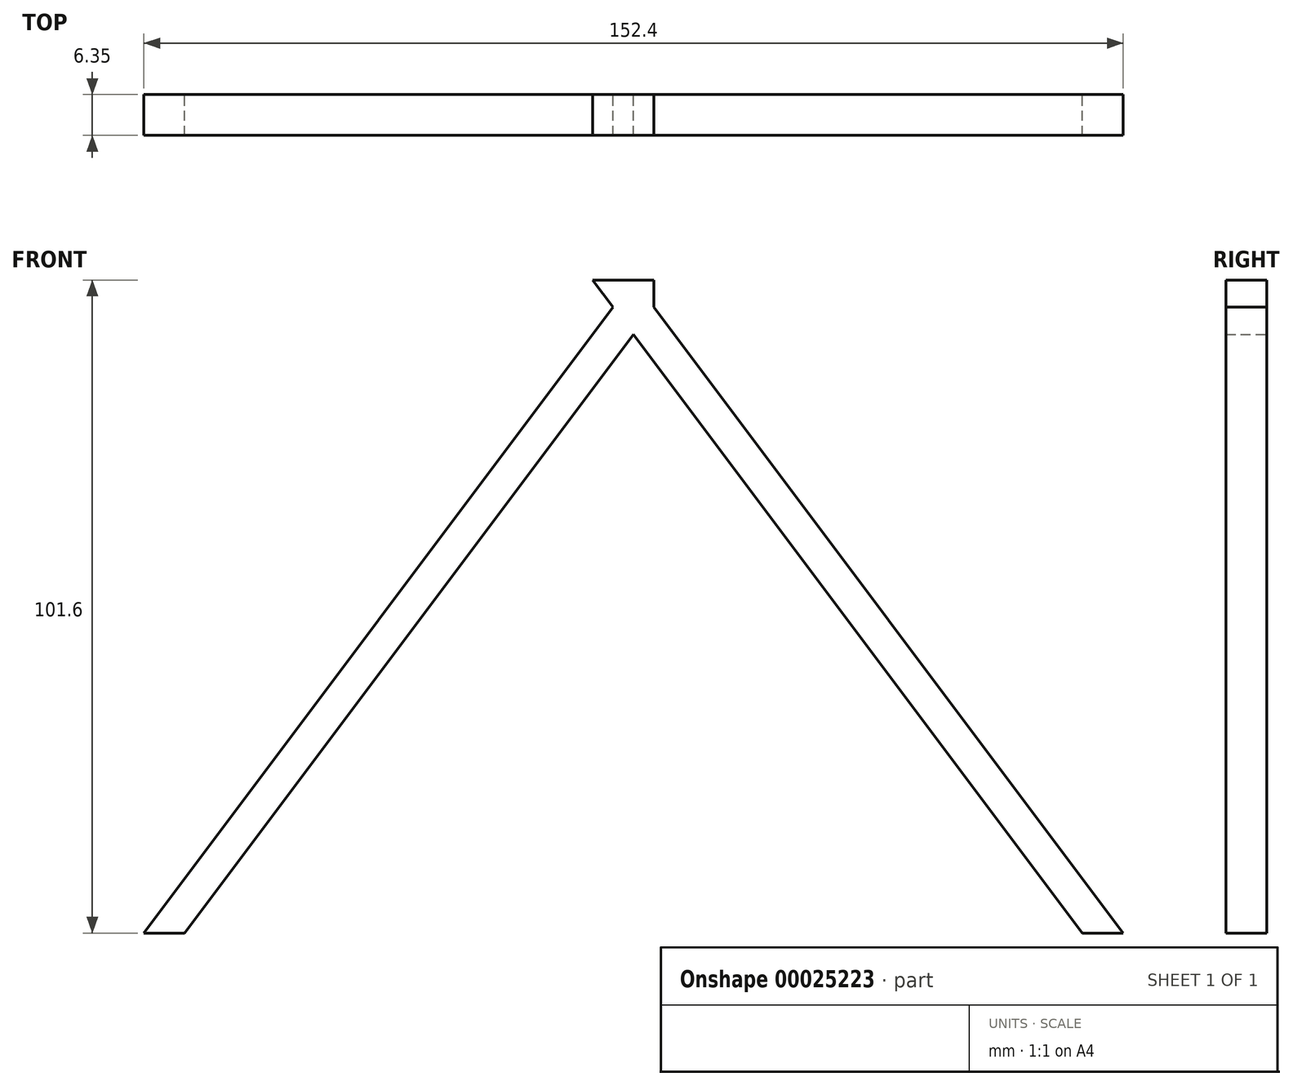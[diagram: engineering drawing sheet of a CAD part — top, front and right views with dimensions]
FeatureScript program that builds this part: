
annotation { "Feature Type Name" : "Feature", "Feature Type Description" : "" }
export const myFeature = defineFeature(function(context is Context, id is Id, definition is map)
    precondition{}
    {
        {
            var Q0;
            Q0=qCreatedBy(makeId("Front.planeOp"),FACE);
            var sketch = newSketch(context, id + "F0", { "sketchPlane" : qUnion([Q0])});
            skLineSegment(sketch, "E0", {"start": v(-76.2, 101.6) * mm, "end": v(0, 0) * mm});
            skLineSegment(sketch, "E1", {"start": v(-76.2, 101.6) * mm, "end": v(-82.55, 101.6) * mm});
            skLineSegment(sketch, "E2", {"start": v(0, 0) * mm, "end": v(-6.35, 0) * mm});
            skLineSegment(sketch, "E3", {"start": v(-6.35, 0) * mm, "end": v(-82.55, 101.6) * mm});
            skLineSegment(sketch, "E4", {"start": v(-82.55, 101.6) * mm, "end": v(-82.55, 101.6) * mm});
            skLineSegment(sketch, "E5", {"start": v(-82.55, 101.6) * mm, "end": v(-79.37, 101.6) * mm});
            skLineSegment(sketch, "E6", {"start": v(-76.2, 106.6) * mm, "end": v(-76.2, -9.76) * mm});
            skLineSegment(sketch, "E7.MirrorCS", {"start": v(-76.2, 101.6) * mm, "end": v(-152.4, 0) * mm});
            skLineSegment(sketch, "E8.MirrorCS", {"start": v(-152.4, 0) * mm, "end": v(-146.05, 0) * mm});
            skLineSegment(sketch, "E9.MirrorCS", {"start": v(-146.05, 0) * mm, "end": v(-69.85, 101.6) * mm});
            skLineSegment(sketch, "E10", {"start": v(-79.37, 101.6) * mm, "end": v(-79.37, 97.37) * mm});
            skLineSegment(sketch, "E11.MirrorCS", {"start": v(-76.2, 101.6) * mm, "end": v(-69.85, 101.6) * mm});
            skLineSegment(sketch, "E12.MirrorCS", {"start": v(-73.03, 101.6) * mm, "end": v(-73.03, 97.37) * mm});
            skSolve(sketch);
        }
        {
            var Q0;
            {var subQ5=sQuery(id+"F0.wireOp",EDGE,"E2");Q0=makeQuery(id+"F0.imprint","IMPRINT",FACE,{"disambiguationData":[TD([[makeQuery(id+"F0.imprint","IMPRINT",EDGE,{"derivedFrom":subQ5}),-1.0]])]});}
            var Q1;
            {var subQ0=sQuery(id+"F0.wireOp",EDGE,"E9.MirrorCS");var subQ3=sQuery(id+"F0.wireOp",EDGE,"E0");var subQ4=makeQuery(id+"F0.imprint","INTERSECT",VERTEX,{"derivedFrom":[subQ3,subQ0]});Q1=makeQuery(id+"F0.imprint","IMPRINT",FACE,{"disambiguationData":[TD([[makeQuery(id+"F0.imprint","IMPRINT",EDGE,{"disambiguationData":[TD([[subQ4,1.0]])],"derivedFrom":subQ0}),1.0]])]});}
            var Q2;
            {var subQ0=sQuery(id+"F0.wireOp",EDGE,"E7.MirrorCS");var subQ1=sQuery(id+"F0.wireOp",EDGE,"E3");var subQ2=makeQuery(id+"F0.imprint","INTERSECT",VERTEX,{"derivedFrom":[subQ1,subQ0]});Q2=makeQuery(id+"F0.imprint","IMPRINT",FACE,{"disambiguationData":[TD([[makeQuery(id+"F0.imprint","IMPRINT",EDGE,{"disambiguationData":[TD([[subQ2,1.0]])],"derivedFrom":subQ1}),-1.0]])]});}
            var Q3;
            {var subQ3=sQuery(id+"F0.wireOp",EDGE,"E8.MirrorCS");Q3=makeQuery(id+"F0.imprint","IMPRINT",FACE,{"disambiguationData":[TD([[makeQuery(id+"F0.imprint","IMPRINT",EDGE,{"derivedFrom":subQ3}),1.0]])]});}
            var Q4;
            {var subQ2=sQuery(id+"F0.wireOp",EDGE,"E1");Q4=makeQuery(id+"F0.imprint","IMPRINT",FACE,{"disambiguationData":[TD([[makeQuery(id+"F0.imprint","IMPRINT",EDGE,{"derivedFrom":subQ2}),1.0]])]});}
            var Q5;
            {var subQ0=sQuery(id+"F0.wireOp",EDGE,"E12.MirrorCS");Q5=makeQuery(id+"F0.imprint","IMPRINT",FACE,{"disambiguationData":[TD([[makeQuery(id+"F0.imprint","IMPRINT",EDGE,{"derivedFrom":subQ0}),-1.0]])]});}
            extrude(context, id + "F1", {"entities" : qUnion([Q0, Q1, Q2, Q3, Q4, Q5]), "depth" : 6.35 * mm});
        }
    });
